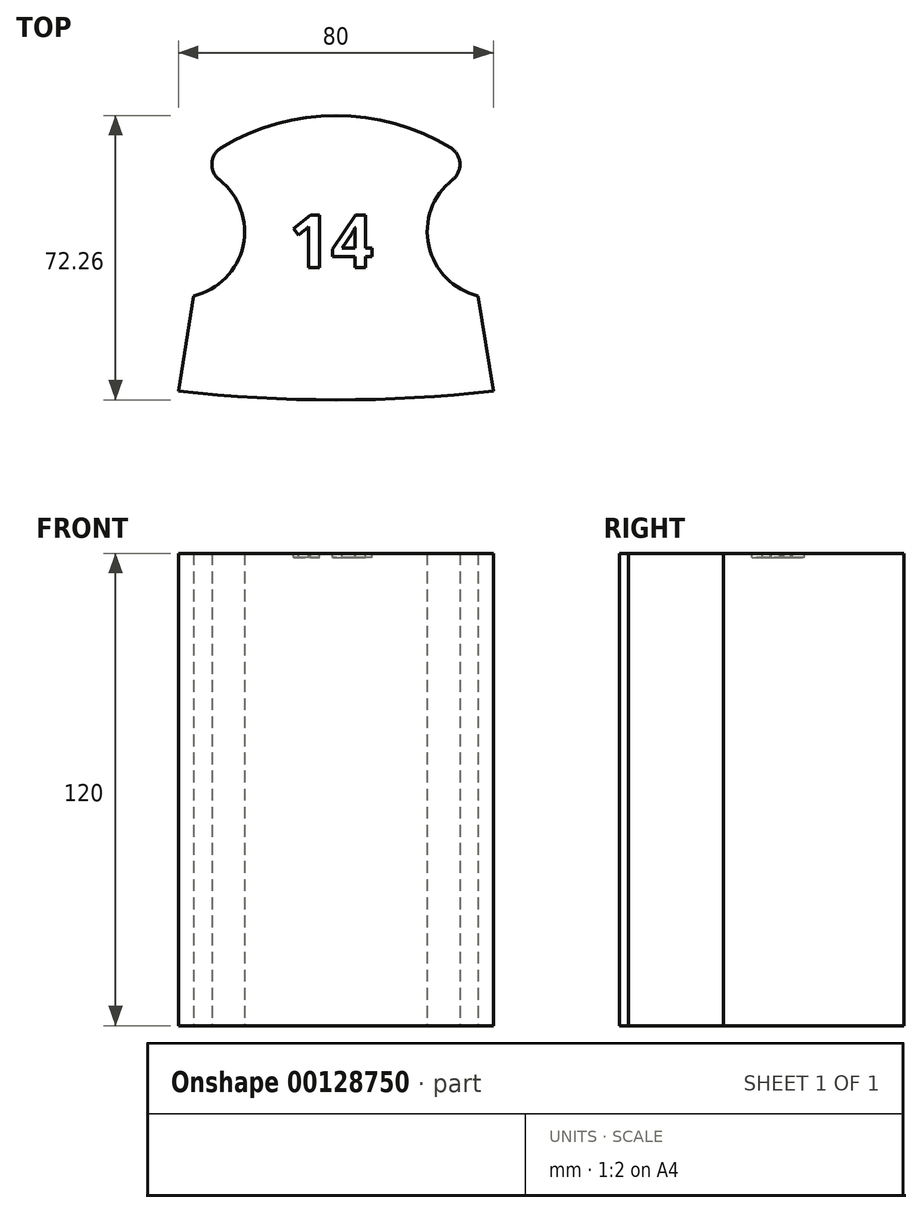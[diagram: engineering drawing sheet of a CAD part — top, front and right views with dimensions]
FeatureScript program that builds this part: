
annotation { "Feature Type Name" : "Feature", "Feature Type Description" : "" }
export const myFeature = defineFeature(function(context is Context, id is Id, definition is map)
    precondition{}
    {
        {
            var Q0;
            Q0=qCreatedBy(makeId("Top.planeOp"),FACE);
            var sketch = newSketch(context, id + "F0", { "sketchPlane" : qUnion([Q0])});
            skLineSegment(sketch, "E0", {"start": v(0, 0) * mm, "end": v(3.87, 24.16) * mm});
            skLineSegment(sketch, "E1", {"start": v(0, 0) * mm, "end": v(80, 0) * mm, "construction": true});
            skLineSegment(sketch, "E2", {"start": v(40, 0) * mm, "end": v(40, 70) * mm, "construction": true});
            skArc(sketch, "E3", {"start": v(3.87, 24.16) * mm, "mid": v(16.4, 36.85) * mm, "end": v(10.4, 53.64) * mm});
            skArc(sketch, "E4.MirrorCS", {"start": v(76.13, 24.16) * mm, "mid": v(63.6, 36.85) * mm, "end": v(69.6, 53.64) * mm});
            skLineSegment(sketch, "E5.MirrorCS", {"start": v(80, 0) * mm, "end": v(76.13, 24.16) * mm});
            skArc(sketch, "E6", {"start": v(69.1, 61.84) * mm, "mid": v(40, 70) * mm, "end": v(10.9, 61.84) * mm});
            skPoint(sketch, "E7.visualSharp", {"position": v(3.87, 56.79) * mm});
            skArc(sketch, "E7.filletArc", {"start": v(10.9, 61.84) * mm, "mid": v(8.5, 57.87) * mm, "end": v(10.4, 53.64) * mm});
            skPoint(sketch, "E8.visualSharp", {"position": v(76.13, 56.79) * mm});
            skArc(sketch, "E8.filletArc", {"start": v(69.6, 53.64) * mm, "mid": v(71.5, 57.87) * mm, "end": v(69.1, 61.84) * mm});
            skArc(sketch, "E9", {"start": v(0, 0) * mm, "mid": v(40, -2.26) * mm, "end": v(80, 0) * mm});
            skSolve(sketch);
        }
        {
            var Q0;
            Q0=makeQuery(id+"F0.imprint","IMPRINT",FACE,{"disambiguationData":[TD([[makeQuery(id+"F0.imprint","IMPRINT",EDGE,{"derivedFrom":sQuery(id+"F0.wireOp",EDGE,"E0")}),-1.0]])]});
            extrude(context, id + "F1", {"entities" : qUnion([Q0]), "depth" : 120 * mm});
        }
        {
            var Q0;
            Q0=makeQuery(id+"F1.opExtrude","CAP_FACE",FACE,{"disambiguationData":[OSD([sQuery(id+"F0.wireOp",EDGE,"E0"),sQuery(id+"F0.wireOp",EDGE,"E3"),sQuery(id+"F0.wireOp",EDGE,"E4.MirrorCS"),sQuery(id+"F0.wireOp",EDGE,"E5.MirrorCS"),sQuery(id+"F0.wireOp",EDGE,"E6"),sQuery(id+"F0.wireOp",EDGE,"E7.filletArc"),sQuery(id+"F0.wireOp",EDGE,"E8.filletArc"),sQuery(id+"F0.wireOp",EDGE,"E9")])],"isStart":false});
            var sketch = newSketch(context, id + "F2", { "sketchPlane" : qUnion([Q0])});
            skText(sketch, "E10", { "text": "14", "fontName": "OpenSans-Bold.ttf"});
            const initialGuessF2  = {"E10": [0.02808, 0.03137, 1, 0, 0.01349]};
            skSetInitialGuess(sketch, initialGuessF2);
            skSolve(sketch);
        }
        {
            var Q0;
            Q0 = qSketchRegion(id + "F2", true);
            extrude(context, id + "F3", {"entities" : qUnion([Q0]), "operationType" : NewBodyOperationType.REMOVE, "oppositeDirection" : true, "depth" : 1 * mm});
        }
    });
